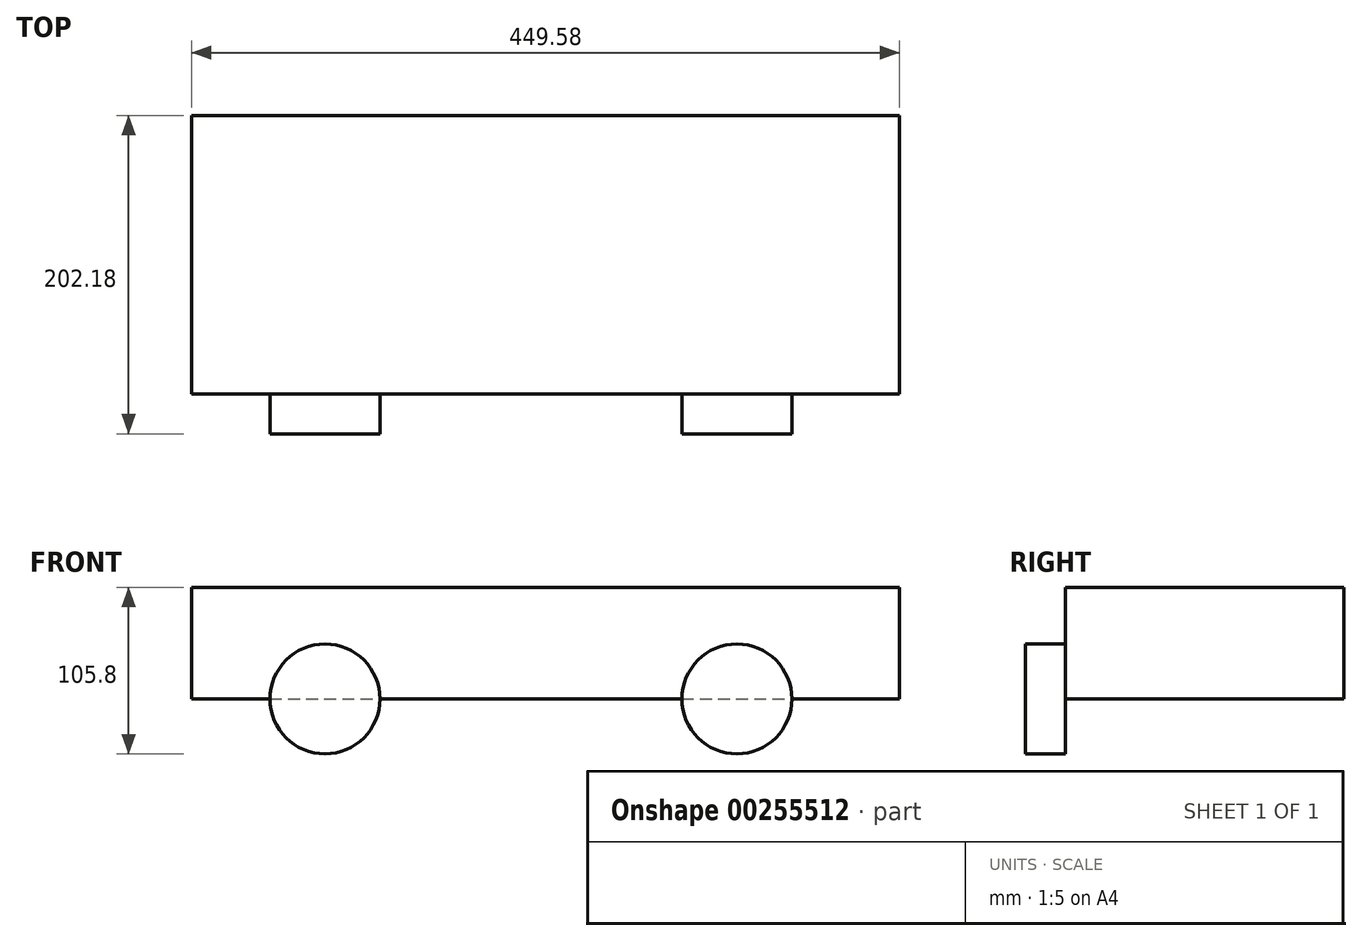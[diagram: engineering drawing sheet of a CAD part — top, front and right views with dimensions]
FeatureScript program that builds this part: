
annotation { "Feature Type Name" : "Feature", "Feature Type Description" : "" }
export const myFeature = defineFeature(function(context is Context, id is Id, definition is map)
    precondition{}
    {
        {
            var Q0;
            Q0=qCreatedBy(makeId("Top.planeOp"),FACE);
            var sketch = newSketch(context, id + "F0", { "sketchPlane" : qUnion([Q0])});
            skLineSegment(sketch, "E0.bottom", {"start": v(-224.12, 122.48) * mm, "end": v(225.46, 122.48) * mm});
            skLineSegment(sketch, "E0.top", {"start": v(-224.12, -54.3) * mm, "end": v(225.46, -54.3) * mm});
            skLineSegment(sketch, "E0.left", {"start": v(-224.12, 122.48) * mm, "end": v(-224.12, -54.3) * mm});
            skLineSegment(sketch, "E0.right", {"start": v(225.46, 122.48) * mm, "end": v(225.46, -54.3) * mm});
            skSolve(sketch);
        }
        {
            var Q0;
            Q0=makeQuery(id+"F0.imprint","IMPRINT",FACE,{"disambiguationData":[TD([[makeQuery(id+"F0.imprint","IMPRINT",EDGE,{"derivedFrom":sQuery(id+"F0.wireOp",EDGE,"E0.bottom")}),-1.0]])]});
            extrude(context, id + "F1", {"entities" : qUnion([Q0]), "depth" : 70.87 * mm});
        }
        {
            var Q0;
            Q0=makeQuery(id+"F1.opExtrude","SWEPT_FACE",FACE,{"disambiguationData":[OSD([sQuery(id+"F0.wireOp",EDGE,"E0.top")])]});
            var sketch = newSketch(context, id + "F2", { "sketchPlane" : qUnion([Q0])});
            skCircle(sketch, "E1", {"center": v(-139.45, 0) * mm, "radius": 34.93 * mm});
            skCircle(sketch, "E2", {"center": v(122.17, 0) * mm, "radius": 34.93 * mm});
            skSolve(sketch);
        }
        {
            var Q0;
            Q0 = qSketchRegion(id + "F2", true);
            extrude(context, id + "F3", {"entities" : qUnion([Q0]), "operationType" : NewBodyOperationType.ADD, "depth" : 25.4 * mm});
        }
    });
